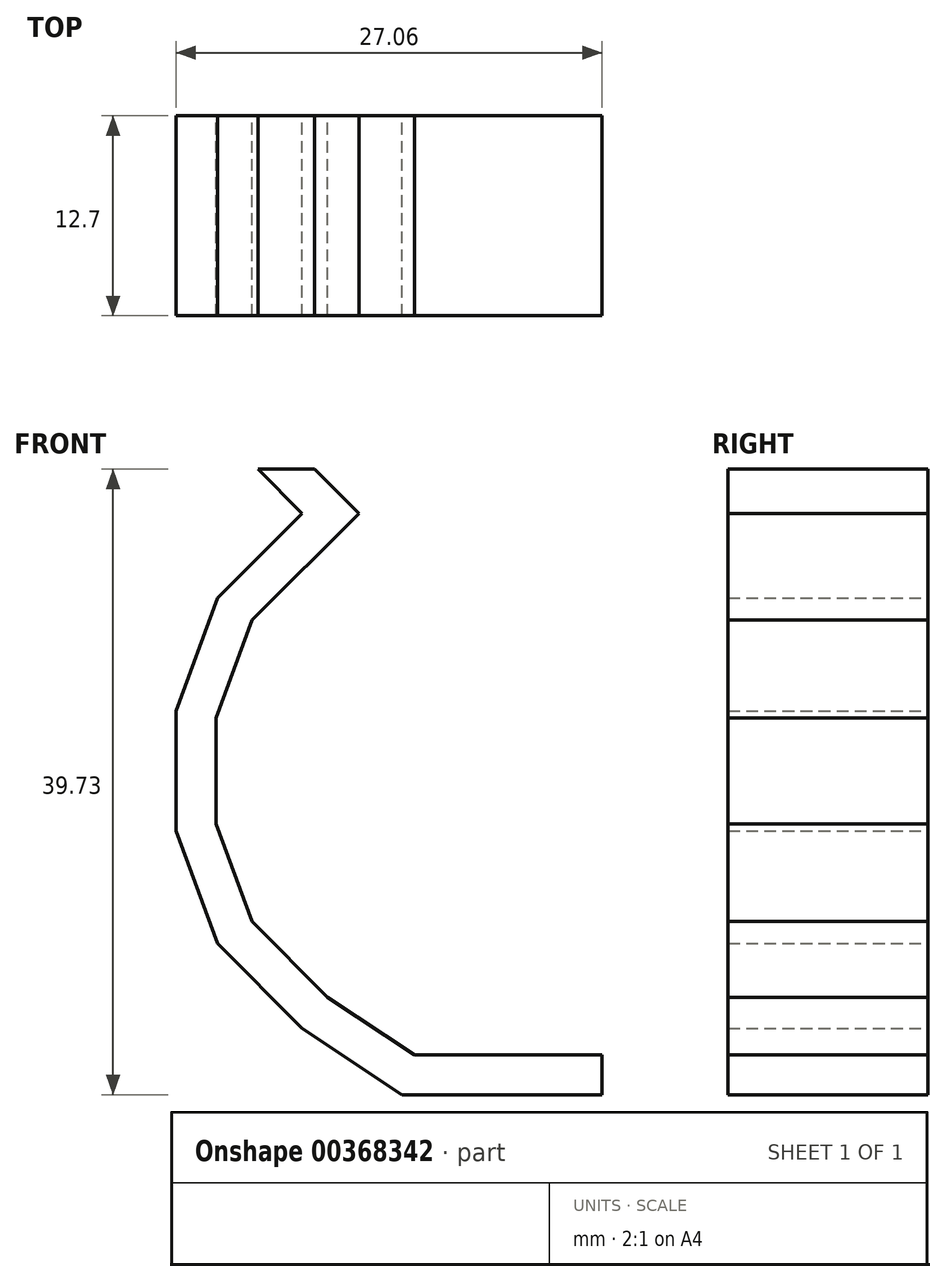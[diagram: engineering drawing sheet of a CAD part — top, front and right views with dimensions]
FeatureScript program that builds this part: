
annotation { "Feature Type Name" : "Feature", "Feature Type Description" : "" }
export const myFeature = defineFeature(function(context is Context, id is Id, definition is map)
    precondition{}
    {
        {
            var Q0;
            Q0=qCreatedBy(makeId("Front.planeOp"),FACE);
            var sketch = newSketch(context, id + "F0", { "sketchPlane" : qUnion([Q0])});
            skLineSegment(sketch, "E0", {"start": v(18.46, -18.52) * mm, "end": v(5.76, -18.52) * mm});
            skLineSegment(sketch, "E1", {"start": v(5.76, -18.52) * mm, "end": v(-0.6, -14.3) * mm});
            skLineSegment(sketch, "E2", {"start": v(-0.6, -14.3) * mm, "end": v(-5.98, -8.92) * mm});
            skLineSegment(sketch, "E3", {"start": v(-5.98, -8.92) * mm, "end": v(-8.6, -1.76) * mm});
            skLineSegment(sketch, "E4", {"start": v(-8.6, -1.76) * mm, "end": v(-8.6, 5.86) * mm});
            skLineSegment(sketch, "E5", {"start": v(-8.6, 5.86) * mm, "end": v(-5.98, 13.01) * mm});
            skLineSegment(sketch, "E6", {"start": v(-5.98, 13.01) * mm, "end": v(-0.6, 18.4) * mm});
            skLineSegment(sketch, "E7", {"start": v(-0.6, 18.4) * mm, "end": v(-3.4, 21.21) * mm});
            skLineSegment(sketch, "E8.0", {"start": v(3, 18.4) * mm, "end": v(0.2, 21.21) * mm});
            skLineSegment(sketch, "E8.1", {"start": v(-3.79, 11.62) * mm, "end": v(3, 18.4) * mm});
            skLineSegment(sketch, "E8.2", {"start": v(-6.06, 5.4) * mm, "end": v(-3.79, 11.62) * mm});
            skLineSegment(sketch, "E8.3", {"start": v(-6.06, -1.31) * mm, "end": v(-6.06, 5.4) * mm});
            skLineSegment(sketch, "E8.4", {"start": v(18.46, -15.98) * mm, "end": v(6.53, -15.98) * mm});
            skLineSegment(sketch, "E8.5", {"start": v(6.53, -15.98) * mm, "end": v(1.03, -12.33) * mm});
            skLineSegment(sketch, "E8.6", {"start": v(1.03, -12.33) * mm, "end": v(-3.79, -7.52) * mm});
            skLineSegment(sketch, "E8.7", {"start": v(-3.79, -7.52) * mm, "end": v(-6.06, -1.31) * mm});
            skLineSegment(sketch, "E9", {"start": v(-3.4, 21.21) * mm, "end": v(0.2, 21.21) * mm});
            skLineSegment(sketch, "E10", {"start": v(18.46, -18.52) * mm, "end": v(18.46, -15.98) * mm});
            skSolve(sketch);
        }
        {
            var Q0;
            Q0 = qSketchRegion(id + "F0", true);
            var Q1;
            Q1=sQuery(id+"F0.wireOp",EDGE,"E0");
            var Q2;
            Q2=sQuery(id+"F0.wireOp",EDGE,"E1");
            var Q3;
            Q3=sQuery(id+"F0.wireOp",EDGE,"E2");
            var Q4;
            Q4=sQuery(id+"F0.wireOp",EDGE,"E3");
            var Q5;
            Q5=sQuery(id+"F0.wireOp",EDGE,"E4");
            var Q6;
            Q6=sQuery(id+"F0.wireOp",EDGE,"E5");
            var Q7;
            Q7=sQuery(id+"F0.wireOp",EDGE,"E6");
            var Q8;
            Q8=sQuery(id+"F0.wireOp",EDGE,"E7");
            var Q9;
            Q9=sQuery(id+"F0.wireOp",EDGE,"E8.0");
            var Q10;
            Q10=sQuery(id+"F0.wireOp",EDGE,"E8.1");
            var Q11;
            Q11=sQuery(id+"F0.wireOp",EDGE,"E8.2");
            var Q12;
            Q12=sQuery(id+"F0.wireOp",EDGE,"E8.3");
            var Q13;
            Q13=sQuery(id+"F0.wireOp",EDGE,"E8.4");
            var Q14;
            Q14=sQuery(id+"F0.wireOp",EDGE,"E8.5");
            var Q15;
            Q15=sQuery(id+"F0.wireOp",EDGE,"E8.6");
            var Q16;
            Q16=sQuery(id+"F0.wireOp",EDGE,"E8.7");
            var Q17;
            Q17=sQuery(id+"F0.wireOp",EDGE,"E9");
            var Q18;
            Q18=sQuery(id+"F0.wireOp",EDGE,"E10");
            extrude(context, id + "F1", {"entities" : qUnion([Q0]), "surfaceEntities" : qUnion([Q1, Q2, Q3, Q4, Q5, Q6, Q7, Q8, Q9, Q10, Q11, Q12, Q13, Q14, Q15, Q16, Q17, Q18]), "endBound" : BoundingType.SYMMETRIC, "depth" : 12.7 * mm});
        }
    });
